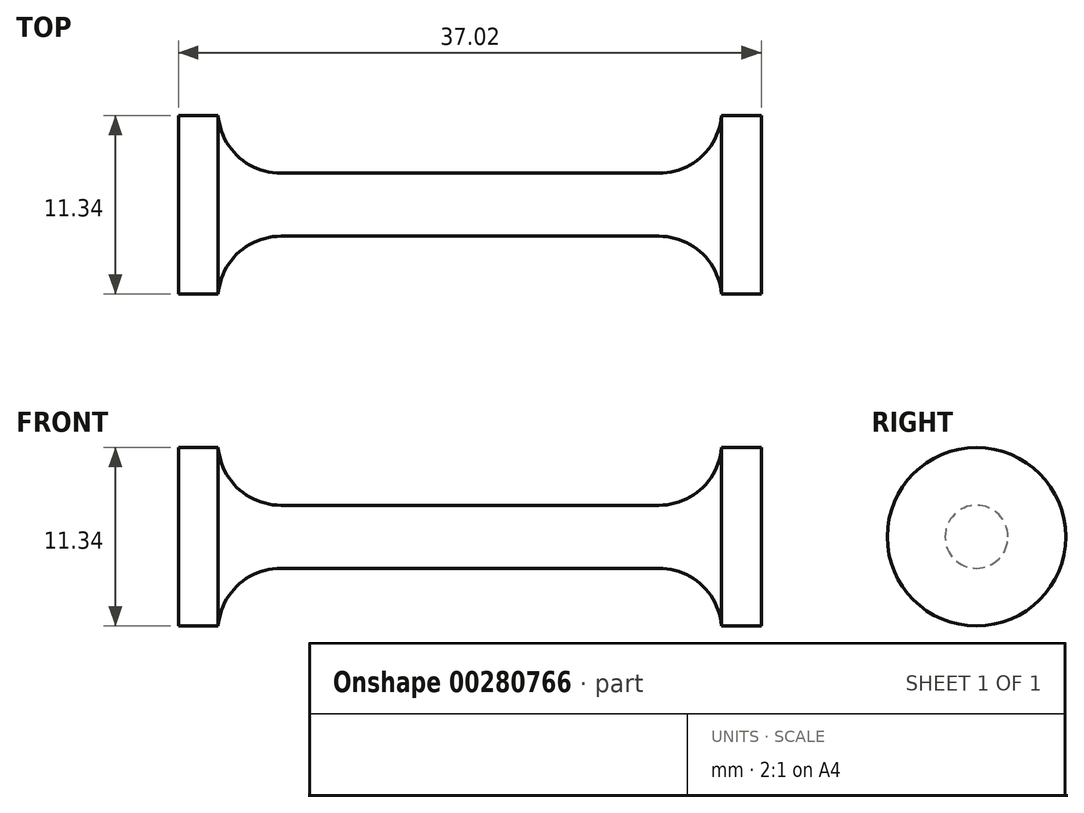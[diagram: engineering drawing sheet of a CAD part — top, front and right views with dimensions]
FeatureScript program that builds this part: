
annotation { "Feature Type Name" : "Feature", "Feature Type Description" : "" }
export const myFeature = defineFeature(function(context is Context, id is Id, definition is map)
    precondition{}
    {
        {
            var Q0;
            Q0=qCreatedBy(makeId("Front.planeOp"),FACE);
            var sketch = newSketch(context, id + "F0", { "sketchPlane" : qUnion([Q0])});
            skLineSegment(sketch, "E0", {"start": v(0, 2) * mm, "end": v(12, 2) * mm});
            skArc(sketch, "E1", {"start": v(12, 2) * mm, "mid": v(14.7, 3.06) * mm, "end": v(15.99, 5.67) * mm});
            skLineSegment(sketch, "E2", {"start": v(15.99, 5.67) * mm, "end": v(18.5, 5.67) * mm});
            skLineSegment(sketch, "E3", {"start": v(18.5, 5.67) * mm, "end": v(18.5, 0) * mm});
            skLineSegment(sketch, "E4.MirrorCS", {"start": v(-15.99, 5.67) * mm, "end": v(-18.5, 5.67) * mm});
            skLineSegment(sketch, "E5.MirrorCS", {"start": v(-18.5, 5.67) * mm, "end": v(-18.5, 0) * mm});
            skLineSegment(sketch, "E6.MirrorCS", {"start": v(0, 2) * mm, "end": v(-12, 2) * mm});
            skArc(sketch, "E7.MirrorCS", {"start": v(-12, 2) * mm, "mid": v(-14.7, 3.06) * mm, "end": v(-15.99, 5.67) * mm});
            skLineSegment(sketch, "E8", {"start": v(-18.5, 0) * mm, "end": v(18.5, 0) * mm});
            skSolve(sketch);
        }
        {
            var Q0;
            Q0 = qSketchRegion(id + "F0", true);
            var Q1;
            Q1=sQuery(id+"F0.wireOp",EDGE,"E8");
            revolve(context, id + "F1", {"entities" : qUnion([Q0]), "axis" : qUnion([Q1]), "revolveType" : RevolveType.FULL});
        }
    });
